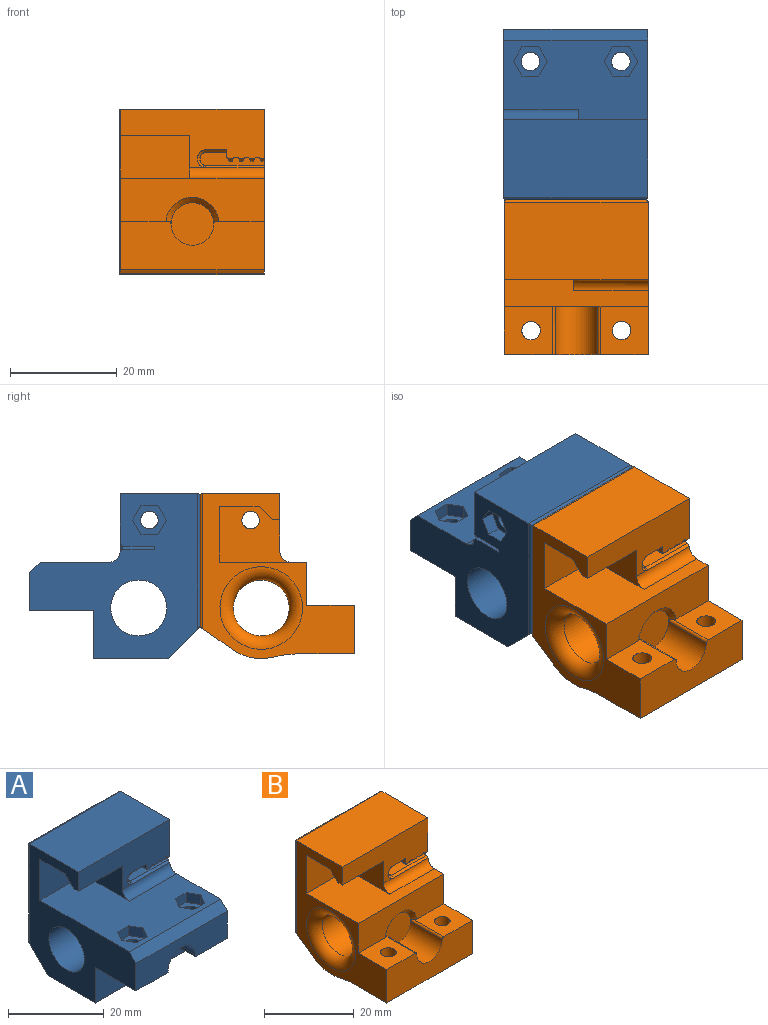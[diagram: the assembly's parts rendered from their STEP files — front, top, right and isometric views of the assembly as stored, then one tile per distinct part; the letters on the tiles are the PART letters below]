
ASSEMBLY  parts=2 mates=1
PART A: 88 faces, bbox 27.2x32.2x31.2 mm
  f0: plane 27x26.4mm, normal (0,0,1), area 472.8mm2, adj f7,f9,f41,f42,f52,f68,f69,f70
  f1: cylinder r=1.75mm len=6.5mm, axis (0,0,-1), area 71.5mm2, adj f67,f76
  f2: cylinder r=1.75mm len=6.5mm, axis (0,0,-1), area 71.5mm2, adj f65,f75
  f3: plane 27x9.6mm, normal (0,-1,0), area 224.6mm2, adj f7,f9,f10,f62,f64,f65,f66,f67
  f4: plane 6x0.51mm, normal (0,0,-1), area 3.1mm2, adj f24,f25,f37,f59
  f5: plane 6x0.51mm, normal (0,0,-1), area 3.1mm2, adj f29,f30,f37,f58
  f6: plane 6x0.51mm, normal (0,0,-1), area 3.1mm2, adj f34,f35,f37,f57
  f7: plane 31.5x31mm, normal (1,0,0), area 514.6mm2, adj f0,f3,f10,f12,f13,f18,f19,f37
  f8: cylinder r=1.65mm len=11.5mm, axis (-1,0,0), area 119.2mm2, adj f42,f50
  f9: plane 31.5x31mm, normal (-1,0,0), area 431.2mm2, adj f0,f3,f10,f12,f13,f38,f39,f40
  f10: plane 27x14mm, normal (0,0,-1), area 378mm2, adj f3,f7,f9,f51
  f11: plane 26x24.5mm, normal (0,1,0), area 631.7mm2, adj f51,f83,f84,f85,f86
  f12: cylinder r=5.25mm len=27mm, axis (-1,0,0), area 890.6mm2, adj f7,f9
  f13: plane 27x14.5mm, normal (0,0,1), area 391.5mm2, adj f7,f9,f43,f85
  f14: cylinder r=0.56mm len=6.5mm, axis (0,-1,0), area 4.1mm2, adj f15,f36,f37,f43,f57
  f15: plane 6.5x1.12mm, normal (-1,0,0), area 4.2mm2, adj f14,f16,f37,f43,f56
  f16: plane 6x4mm, normal (0,0,-1), area 24mm2, adj f15,f17,f37,f56
  f17: cylinder r=1mm len=6mm, axis (0,-1,0), area 18.9mm2, adj f16,f18,f37,f54,f55
  f18: plane 11x6mm, normal (0,0,1), area 66mm2, adj f7,f17,f37,f53
  f19: plane 6x0.25mm, normal (0,0,-1), area 1.5mm2, adj f7,f20,f37,f60
  f20: cylinder r=0.15mm len=6.13mm, axis (0,-1,0), area 1.3mm2, adj f19,f21,f37,f60
  f21: cylinder r=1mm len=6.43mm, axis (0,-1,0), area 2mm2, adj f20,f22,f37,f60
  f22: cylinder r=0.56mm len=6.5mm, axis (0,-1,0), area 8.2mm2, adj f21,f23,f37,f43,f59,f60
  f23: cylinder r=1mm len=6.43mm, axis (0,-1,0), area 2mm2, adj f22,f24,f37,f59
  f24: cylinder r=0.15mm len=6.13mm, axis (0,-1,0), area 1.3mm2, adj f4,f23,f37,f59
  f25: cylinder r=0.15mm len=6.13mm, axis (0,-1,0), area 1.3mm2, adj f4,f26,f37,f59
  f26: cylinder r=1mm len=6.43mm, axis (0,-1,0), area 2mm2, adj f25,f27,f37,f59
  f27: cylinder r=0.56mm len=6.5mm, axis (0,-1,0), area 8.2mm2, adj f26,f28,f37,f43,f58,f59
  f28: cylinder r=1mm len=6.43mm, axis (0,-1,0), area 2mm2, adj f27,f29,f37,f58
  f29: cylinder r=0.15mm len=6.13mm, axis (0,-1,0), area 1.3mm2, adj f5,f28,f37,f58
  f30: cylinder r=0.15mm len=6.13mm, axis (0,-1,0), area 1.3mm2, adj f5,f31,f37,f58
  f31: cylinder r=1mm len=6.43mm, axis (0,-1,0), area 2mm2, adj f30,f32,f37,f58
  f32: cylinder r=0.56mm len=6.5mm, axis (0,-1,0), area 8.2mm2, adj f31,f33,f37,f43,f57,f58
  f33: cylinder r=1mm len=6.43mm, axis (0,-1,0), area 2mm2, adj f32,f34,f37,f57
  f34: cylinder r=0.15mm len=6.13mm, axis (0,-1,0), area 1.3mm2, adj f6,f33,f37,f57
  f35: cylinder r=0.15mm len=6.13mm, axis (0,-1,0), area 1.3mm2, adj f6,f36,f37,f57
  f36: cylinder r=1mm len=6.43mm, axis (0,-1,0), area 2mm2, adj f14,f35,f37,f57
  f37: plane 12x2mm, normal (0,-1,0), area 16.5mm2, adj f4,f5,f6,f7,f14,f15,f16,f17
  f38: plane 13x1.4mm, normal (0,0,-1), area 18.2mm2, adj f9,f39,f42,f43
  f39: plane 13x2.5mm, normal (0,0.71,-0.71), area 46mm2, adj f9,f38,f40,f42
  f40: plane 13x7.5mm, normal (0,0,-1), area 97.5mm2, adj f9,f39,f41,f42
  f41: plane 13x10.5mm, normal (0,-1,0), area 136.5mm2, adj f0,f9,f40,f42
  f42: plane 13.4x10.5mm, normal (-1,0,0), area 105.4mm2, adj f0,f8,f38,f39,f40,f41,f43,f52
  f43: plane 27x10.9mm, normal (0,-1,0), area 189.9mm2, adj f7,f9,f13,f14,f15,f22,f27,f32
  f44: plane 2.75x2.5mm, normal (0,-0.87,0.5), area 7.9mm2, adj f7,f45,f49,f50
  f45: plane 2.75x2.5mm, normal (0,-0.87,-0.5), area 7.9mm2, adj f7,f44,f46,f50
  f46: plane 3.18x2.5mm, normal (0,0,-1), area 7.9mm2, adj f7,f45,f47,f50
  f47: plane 2.75x2.5mm, normal (0,0.87,-0.5), area 7.9mm2, adj f7,f46,f48,f50
  f48: plane 2.75x2.5mm, normal (0,0.87,0.5), area 7.9mm2, adj f7,f47,f49,f50
  f49: plane 3.18x2.5mm, normal (0,0,1), area 7.9mm2, adj f7,f44,f48,f50
  f50: plane 6.35x5.5mm, normal (1,0,0), area 17.6mm2, adj f8,f44,f45,f46,f47,f48,f49
  f51: plane 27.21x6.21mm, normal (0,0.71,-0.71), area 229mm2, adj f7,f9,f10,f11,f83,f84
  f52: cylinder r=2mm len=14mm, axis (-1,0,0), area 43.1mm2, adj f0,f7,f42,f43,f53,f54
  f53: plane 11x0.5mm, normal (0,-0.69,0.72), area 7.6mm2, adj f7,f18,f52,f54
  f54: bspline ~0.55x0.54mm, area 0.3mm2, adj f17,f52,f53,f55
  f55: cone r=1mm half-angle=45deg, axis (0,-1,0), area 2.5mm2, adj f17,f43,f54,f56
  f56: plane 4x0.5mm, normal (0,-0.71,-0.71), area 2.8mm2, adj f15,f16,f43,f55
  f57: plane 1.12x0.56mm, normal (0,-0.71,-0.71), area 0.6mm2, adj f6,f14,f32,f33,f34,f35,f36,f43
  f58: plane 1.12x0.56mm, normal (0,-0.71,-0.71), area 0.6mm2, adj f5,f27,f28,f29,f30,f31,f32,f43
  f59: plane 1.12x0.56mm, normal (0,-0.71,-0.71), area 0.6mm2, adj f4,f22,f23,f24,f25,f26,f27,f43
  f60: plane 0.59x0.56mm, normal (0,-0.71,-0.71), area 0.3mm2, adj f7,f19,f20,f21,f22,f43
  f61: plane 27x7mm, normal (0,-1,0), area 159.9mm2, adj f7,f9,f62,f64,f65,f66,f67,f68
  f62: cylinder r=4mm len=13mm, axis (0,-1,0), area 175.9mm2, adj f3,f61,f63,f64,f66
  f63: plane 8x8mm, normal (0,-1,0), area 50.3mm2, adj f62
  f64: plane 12x0.5mm, normal (1,0,0), area 6mm2, adj f3,f61,f62,f65
  f65: plane 12x9.5mm, normal (0,0,-1), area 104.4mm2, adj f2,f3,f9,f61,f64
  f66: plane 12x0.5mm, normal (-1,0,0), area 6mm2, adj f3,f61,f62,f67
  f67: plane 12x9.5mm, normal (0,0,-1), area 104.4mm2, adj f1,f3,f7,f61,f66
  f68: plane 27x2mm, normal (0,-0.71,0.71), area 76.4mm2, adj f0,f7,f9,f61
  f69: plane 2.75x2.5mm, normal (-0.87,-0.5,0), area 7.9mm2, adj f0,f70,f74,f75
  f70: plane 3.18x2.5mm, normal (0,-1,0), area 7.9mm2, adj f0,f69,f71,f75
  f71: plane 2.75x2.5mm, normal (0.87,-0.5,0), area 7.9mm2, adj f0,f70,f72,f75
  f72: plane 2.75x2.5mm, normal (0.87,0.5,0), area 7.9mm2, adj f0,f71,f73,f75
  f73: plane 3.18x2.5mm, normal (0,1,0), area 7.9mm2, adj f0,f72,f74,f75
  f74: plane 2.75x2.5mm, normal (-0.87,0.5,0), area 7.9mm2, adj f0,f69,f73,f75
  f75: plane 6.35x5.5mm, normal (0,0,1), area 16.6mm2, adj f2,f69,f70,f71,f72,f73,f74
  f76: plane 6.35x5.5mm, normal (0,0,1), area 16.6mm2, adj f1,f77,f78,f79,f80,f81,f82
  f77: plane 2.75x2.5mm, normal (-0.87,0.5,0), area 7.9mm2, adj f0,f76,f78,f82
  f78: plane 2.75x2.5mm, normal (-0.87,-0.5,0), area 7.9mm2, adj f0,f76,f77,f79
  f79: plane 3.18x2.5mm, normal (0,-1,0), area 7.9mm2, adj f0,f76,f78,f80
  f80: plane 2.75x2.5mm, normal (0.87,-0.5,0), area 7.9mm2, adj f0,f76,f79,f81
  f81: plane 2.75x2.5mm, normal (0.87,0.5,0), area 7.9mm2, adj f0,f76,f80,f82
  f82: plane 3.18x2.5mm, normal (0,1,0), area 7.9mm2, adj f0,f76,f77,f81
  f83: cylinder r=0.5mm len=25.5mm, axis (0,0,-1), area 19.6mm2, adj f7,f11,f51,f85
  f84: cylinder r=0.5mm len=25.5mm, axis (0,0,1), area 19.6mm2, adj f9,f11,f51,f85
  f85: cylinder r=0.5mm len=27mm, axis (-1,0,0), area 20.8mm2, adj f11,f13,f83,f84
  f86: cylinder r=1.3mm len=12mm, axis (0,1,0), area 98mm2, adj f11,f87
  f87: plane 2.6x2.6mm, normal (0,1,0), area 5.3mm2, adj f86
PART B: 97 faces, bbox 27.1x29.1x31.9 mm
  f0: plane 27x10.27mm, normal (0,0,-1), area 224.9mm2, adj f4,f5,f58,f66,f67,f68,f69,f70
  f1: cylinder r=1.75mm len=6.6mm, axis (0,0,1), area 72.6mm2, adj f62,f78
  f2: cylinder r=1.75mm len=6.6mm, axis (0,0,1), area 72.6mm2, adj f61,f65
  f3: plane 26x24.28mm, normal (0,1,0), area 626.1mm2, adj f79,f80,f81,f82,f83
  f4: plane 31x28.5mm, normal (1,0,0), area 374.3mm2, adj f0,f10,f11,f19,f20,f38,f39,f45
  f5: plane 31x28.5mm, normal (-1,0,0), area 292mm2, adj f0,f10,f11,f39,f40,f41,f42,f43
  f6: plane 6x0.39mm, normal (0,0,-1), area 2.3mm2, adj f25,f26,f38,f56
  f7: plane 6x0.39mm, normal (0,0,-1), area 2.3mm2, adj f30,f31,f38,f55
  f8: plane 6x0.39mm, normal (0,0,-1), area 2.3mm2, adj f35,f36,f38,f54
  f9: cylinder r=1.65mm len=11.5mm, axis (-1,0,0), area 119.2mm2, adj f44,f52
  f10: plane 27x8.1mm, normal (0,-1,0), area 184.4mm2, adj f4,f5,f39,f61,f62,f93
  f11: plane 27x14.5mm, normal (0,0,1), area 391.5mm2, adj f4,f5,f45,f79
  f12: cylinder r=5.25mm len=22mm, axis (-1,0,0), area 725.7mm2, adj f85,f86
  f13: cylinder r=0.65mm len=6.5mm, axis (0,-1,0), area 3.4mm2, adj f14,f37,f38,f45,f54
  f14: plane 6.5x1.42mm, normal (-1,0,0), area 6.1mm2, adj f13,f15,f38,f45,f92
  f15: plane 6x4mm, normal (0,0,-1), area 24mm2, adj f14,f16,f38,f92
  f16: cylinder r=1mm len=6mm, axis (0,-1,0), area 9.4mm2, adj f15,f17,f38,f91
  f17: plane 6x0.4mm, normal (1,0,0), area 2.4mm2, adj f16,f18,f38,f90
  f18: cylinder r=1mm len=6mm, axis (0,-1,0), area 9.4mm2, adj f17,f19,f38,f88,f89
  f19: plane 11x6mm, normal (0,0,1), area 66mm2, adj f4,f18,f38,f87
  f20: plane 6x0.5mm, normal (0,0,-1), area 3mm2, adj f4,f21,f38,f57
  f21: cylinder r=0.15mm len=6.13mm, axis (0,-1,0), area 1.3mm2, adj f20,f22,f38,f57
  f22: cylinder r=1mm len=6.29mm, axis (0,-1,0), area 1mm2, adj f21,f23,f38,f57
  f23: cylinder r=0.65mm len=6.5mm, axis (0,-1,0), area 10.8mm2, adj f22,f24,f38,f45,f56,f57
  f24: cylinder r=1mm len=6.29mm, axis (0,-1,0), area 1mm2, adj f23,f25,f38,f56
  f25: cylinder r=0.15mm len=6.13mm, axis (0,-1,0), area 1.3mm2, adj f6,f24,f38,f56
  f26: cylinder r=0.15mm len=6.13mm, axis (0,-1,0), area 1.3mm2, adj f6,f27,f38,f56
  f27: cylinder r=1mm len=6.29mm, axis (0,-1,0), area 1mm2, adj f26,f28,f38,f56
  f28: cylinder r=0.65mm len=6.5mm, axis (0,-1,0), area 10.8mm2, adj f27,f29,f38,f45,f55,f56
  f29: cylinder r=1mm len=6.29mm, axis (0,-1,0), area 1mm2, adj f28,f30,f38,f55
  f30: cylinder r=0.15mm len=6.13mm, axis (0,-1,0), area 1.3mm2, adj f7,f29,f38,f55
  f31: cylinder r=0.15mm len=6.13mm, axis (0,-1,0), area 1.3mm2, adj f7,f32,f38,f55
  f32: cylinder r=1mm len=6.29mm, axis (0,-1,0), area 1mm2, adj f31,f33,f38,f55
  f33: cylinder r=0.65mm len=6.5mm, axis (0,-1,0), area 10.8mm2, adj f32,f34,f38,f45,f54,f55
  f34: cylinder r=1mm len=6.29mm, axis (0,-1,0), area 1mm2, adj f33,f35,f38,f54
  f35: cylinder r=0.15mm len=6.13mm, axis (0,-1,0), area 1.3mm2, adj f8,f34,f38,f54
  f36: cylinder r=0.15mm len=6.13mm, axis (0,-1,0), area 1.3mm2, adj f8,f37,f38,f54
  f37: cylinder r=1mm len=6.29mm, axis (0,-1,0), area 1mm2, adj f13,f36,f38,f54
  f38: plane 12x2.4mm, normal (0,-1,0), area 19.8mm2, adj f4,f6,f7,f8,f13,f14,f15,f16
  f39: plane 27x16.4mm, normal (0,0,1), area 255.2mm2, adj f4,f5,f10,f43,f44,f53
  f40: plane 13x1.4mm, normal (0,0,-1), area 18.2mm2, adj f5,f41,f44,f45
  f41: plane 13x2.5mm, normal (0,0.71,-0.71), area 46mm2, adj f5,f40,f42,f44
  f42: plane 13x7.5mm, normal (0,0,-1), area 97.5mm2, adj f5,f41,f43,f44
  f43: plane 13x10.5mm, normal (0,-1,0), area 136.5mm2, adj f5,f39,f42,f44
  f44: plane 13.4x10.5mm, normal (-1,0,0), area 105.4mm2, adj f9,f39,f40,f41,f42,f43,f45,f53
  f45: plane 27x10.9mm, normal (0,-1,0), area 186.5mm2, adj f4,f5,f11,f13,f14,f23,f28,f33
  f46: plane 3.18x2.5mm, normal (0,0,1), area 7.9mm2, adj f4,f47,f51,f52
  f47: plane 2.75x2.5mm, normal (0,-0.87,0.5), area 7.9mm2, adj f4,f46,f48,f52
  f48: plane 2.75x2.5mm, normal (0,-0.87,-0.5), area 7.9mm2, adj f4,f47,f49,f52
  f49: plane 3.18x2.5mm, normal (0,0,-1), area 7.9mm2, adj f4,f48,f50,f52
  f50: plane 2.75x2.5mm, normal (0,0.87,-0.5), area 7.9mm2, adj f4,f49,f51,f52
  f51: plane 2.75x2.5mm, normal (0,0.87,0.5), area 7.9mm2, adj f4,f46,f50,f52
  f52: plane 6.35x5.5mm, normal (1,0,0), area 17.6mm2, adj f9,f46,f47,f48,f49,f50,f51
  f53: cylinder r=2mm len=14mm, axis (-1,0,0), area 43.1mm2, adj f4,f39,f44,f45,f87,f88
  f54: plane 1.03x0.56mm, normal (0,-0.71,-0.71), area 0.5mm2, adj f8,f13,f33,f34,f35,f36,f37,f45
  f55: plane 1.03x0.56mm, normal (0,-0.71,-0.71), area 0.5mm2, adj f7,f28,f29,f30,f31,f32,f33,f45
  f56: plane 1.03x0.56mm, normal (0,-0.71,-0.71), area 0.5mm2, adj f6,f23,f24,f25,f26,f27,f28,f45
  f57: plane 0.84x0.56mm, normal (0,-0.71,-0.71), area 0.5mm2, adj f4,f20,f21,f22,f23,f45
  f58: plane 27x9.1mm, normal (0,-1,0), area 216.5mm2, adj f0,f4,f5,f59,f61,f62,f94,f95
  f59: cylinder r=4mm len=10mm, axis (0,-1,0), area 125.7mm2, adj f58,f60,f94,f95
  f60: plane 8x8mm, normal (0,-1,0), area 50.3mm2, adj f59,f93
  f61: plane 9.47x9mm, normal (0,0,1), area 71.5mm2, adj f2,f5,f10,f58,f93,f95
  f62: plane 9.47x9mm, normal (0,0,1), area 71.5mm2, adj f1,f4,f10,f58,f93,f94
  f63: cylinder r=9.5mm len=27mm, axis (-1,0,0), area 220.2mm2, adj f4,f5,f64,f96
  f64: plane 27.01x5.85mm, normal (0,0.57,-0.82), area 192.4mm2, adj f4,f5,f63,f80,f81,f82
  f65: plane 6.35x5.5mm, normal (0,0,-1), area 16.6mm2, adj f2,f66,f67,f68,f69,f70,f71
  f66: plane 3.18x2.5mm, normal (-1,0,0), area 7.9mm2, adj f0,f65,f67,f71
  f67: plane 2.75x2.5mm, normal (-0.5,0.87,0), area 7.9mm2, adj f0,f65,f66,f68
  f68: plane 2.75x2.5mm, normal (0.5,0.87,0), area 7.9mm2, adj f0,f65,f67,f69
  f69: plane 3.18x2.5mm, normal (1,0,0), area 7.9mm2, adj f0,f65,f68,f70
  f70: plane 2.75x2.5mm, normal (0.5,-0.87,0), area 7.9mm2, adj f0,f65,f69,f71
  f71: plane 2.75x2.5mm, normal (-0.5,-0.87,0), area 7.9mm2, adj f0,f65,f66,f70
  f72: plane 2.75x2.5mm, normal (-0.5,-0.87,0), area 7.9mm2, adj f0,f73,f77,f78
  f73: plane 3.18x2.5mm, normal (-1,0,0), area 7.9mm2, adj f0,f72,f74,f78
  f74: plane 2.75x2.5mm, normal (-0.5,0.87,0), area 7.9mm2, adj f0,f73,f75,f78
  f75: plane 2.75x2.5mm, normal (0.5,0.87,0), area 7.9mm2, adj f0,f74,f76,f78
  f76: plane 3.18x2.5mm, normal (1,0,0), area 7.9mm2, adj f0,f75,f77,f78
  f77: plane 2.75x2.5mm, normal (0.5,-0.87,0), area 7.9mm2, adj f0,f72,f76,f78
  f78: plane 6.35x5.5mm, normal (0,0,-1), area 16.6mm2, adj f1,f72,f73,f74,f75,f76,f77
  f79: cylinder r=0.5mm len=27mm, axis (-1,0,0), area 20.8mm2, adj f3,f11,f80,f81
  f80: cylinder r=0.5mm len=25.4mm, axis (0,0,-1), area 19.5mm2, adj f3,f4,f64,f79,f82
  f81: cylinder r=0.5mm len=25.4mm, axis (0,0,1), area 19.5mm2, adj f3,f5,f64,f79,f82
  f82: cylinder r=0.5mm len=26.82mm, axis (1,0,0), area 12.7mm2, adj f3,f64,f80,f81
  f83: cylinder r=1.3mm len=12mm, axis (0,1,0), area 98mm2, adj f3,f84
  f84: plane 2.6x2.6mm, normal (0,1,0), area 5.3mm2, adj f83
  f85: torus R=7.75mm, axis (1,0,0), area 152mm2, adj f5,f12
  f86: torus R=7.75mm, axis (1,0,0), area 152mm2, adj f4,f12
  f87: plane 11x0.5mm, normal (0,-0.69,0.72), area 7.6mm2, adj f4,f19,f53,f88
  f88: bspline ~0.55x0.54mm, area 0.3mm2, adj f18,f53,f87,f89
  f89: cone r=1mm half-angle=45deg, axis (0,-1,0), area 1.1mm2, adj f18,f45,f88,f90
  f90: plane 0.5x0.5mm, normal (0.71,-0.71,0), area 0.3mm2, adj f17,f45,f89,f91
  f91: cone r=1mm half-angle=45deg, axis (0,-1,0), area 1.4mm2, adj f16,f45,f90,f92
  f92: plane 4x0.5mm, normal (0,-0.71,-0.71), area 2.8mm2, adj f14,f15,f45,f91
  f93: cone r=5mm half-angle=45deg, axis (0,-1,0), area 18.7mm2, adj f10,f60,f61,f62,f94,f95
  f94: cylinder r=0.5mm len=10mm, axis (0,1,0), area 7.6mm2, adj f58,f59,f62,f93
  f95: cylinder r=0.5mm len=10mm, axis (0,1,0), area 7.6mm2, adj f58,f59,f61,f93
  f96: cylinder r=20mm len=27mm, axis (-1,0,0), area 133.7mm2, adj f0,f4,f5,f63
PLACE A rot(axis=(0,0,1),180deg) t=(-0.13,35,0)mm
PLACE B at identity
MATE parallel A.f11 <-> B.f3  axis (0,-1,0) through (-0.07,17.5,2.26)mm
